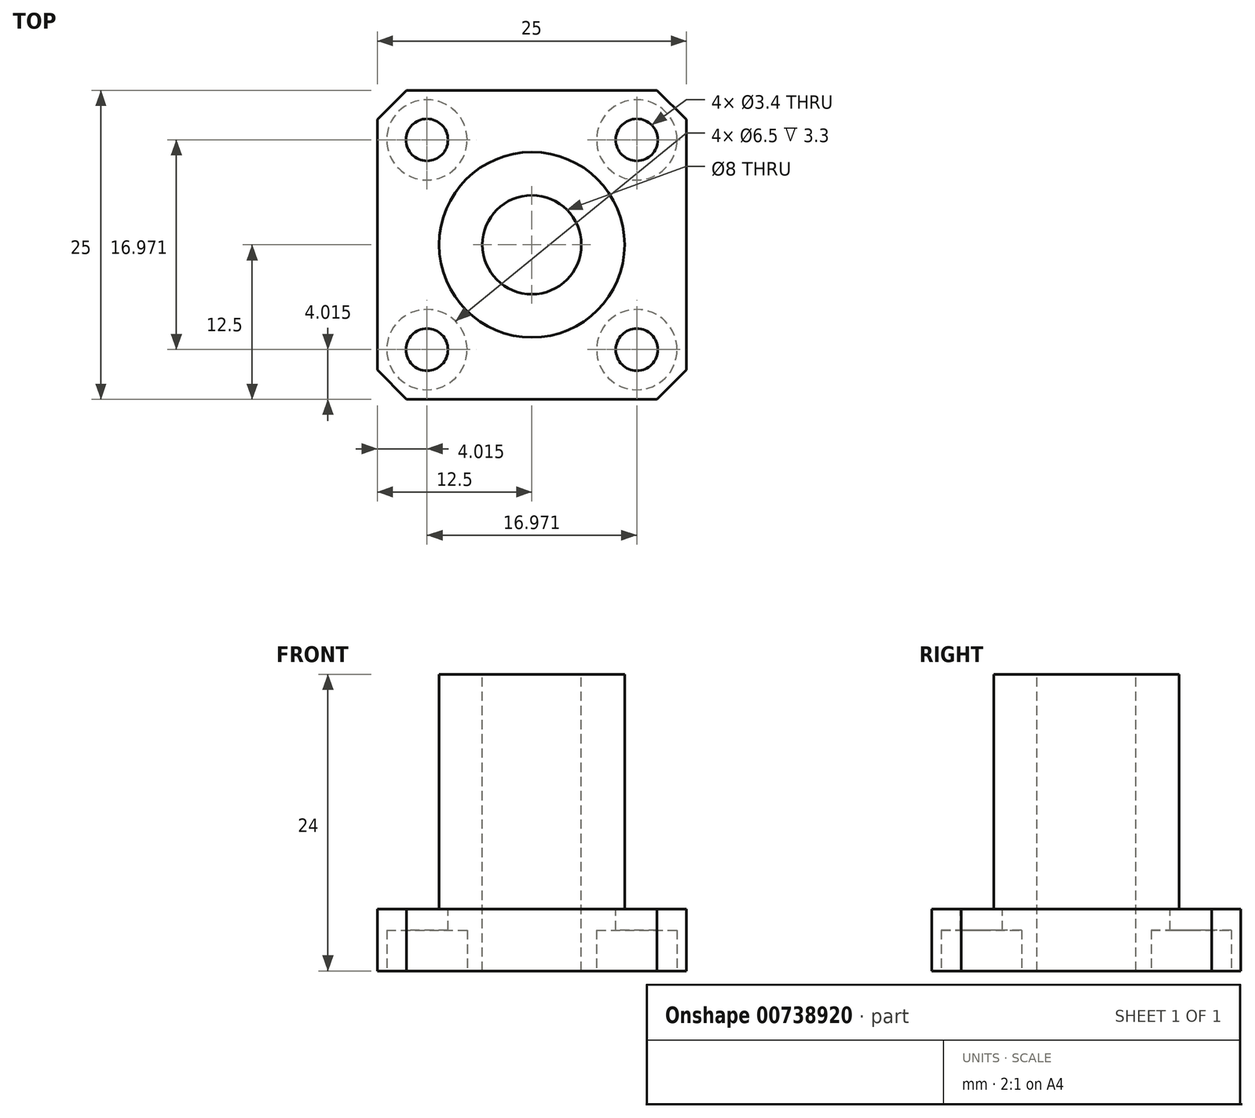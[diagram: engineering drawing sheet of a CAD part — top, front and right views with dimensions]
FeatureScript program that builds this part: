
annotation { "Feature Type Name" : "Feature", "Feature Type Description" : "" }
export const myFeature = defineFeature(function(context is Context, id is Id, definition is map)
    precondition{}
    {
        {
            var Q0;
            Q0=qCreatedBy(makeId("Top.planeOp"),FACE);
            var sketch = newSketch(context, id + "F0", { "sketchPlane" : qUnion([Q0])});
            skCircle(sketch, "E0", {"center": v(0, 0) * mm, "radius": 7.5 * mm});
            skCircle(sketch, "E1", {"center": v(0, 0) * mm, "radius": 4 * mm});
            skLineSegment(sketch, "E2.bottom", {"start": v(12.5, 12.5) * mm, "end": v(-12.5, 12.5) * mm});
            skLineSegment(sketch, "E2.top", {"start": v(12.5, -12.5) * mm, "end": v(-12.5, -12.5) * mm});
            skLineSegment(sketch, "E2.left", {"start": v(12.5, 12.5) * mm, "end": v(12.5, -12.5) * mm});
            skLineSegment(sketch, "E2.right", {"start": v(-12.5, 12.5) * mm, "end": v(-12.5, -12.5) * mm});
            skPoint(sketch, "E3", {"position": v(-8.49, -8.49) * mm});
            skPoint(sketch, "E4", {"position": v(8.49, 8.49) * mm});
            skPoint(sketch, "E5", {"position": v(-8.49, 8.49) * mm});
            skPoint(sketch, "E6", {"position": v(8.49, -8.49) * mm});
            skCircle(sketch, "E7", {"center": v(-8.49, 8.49) * mm, "radius": 1.7 * mm});
            skCircle(sketch, "E8", {"center": v(8.49, 8.49) * mm, "radius": 1.7 * mm});
            skCircle(sketch, "E9", {"center": v(8.49, -8.49) * mm, "radius": 1.7 * mm});
            skCircle(sketch, "E10", {"center": v(-8.49, -8.49) * mm, "radius": 1.7 * mm});
            skCircle(sketch, "E11", {"center": v(0, 0) * mm, "radius": 12 * mm, "construction": true});
            skLineSegment(sketch, "E12", {"start": v(-12.5, 12.5) * mm, "end": v(12.5, -12.5) * mm, "construction": true});
            skLineSegment(sketch, "E13", {"start": v(12.5, 12.5) * mm, "end": v(-12.5, -12.5) * mm, "construction": true});
            skSolve(sketch);
        }
        {
            var Q0;
            Q0=makeQuery(id+"F0.imprint","IMPRINT",FACE,{"disambiguationData":[TD([[makeQuery(id+"F0.imprint","IMPRINT",EDGE,{"derivedFrom":sQuery(id+"F0.wireOp",EDGE,"E0")}),1.0]])]});
            var Q1;
            Q1=makeQuery(id+"F0.imprint","IMPRINT",FACE,{"disambiguationData":[TD([[makeQuery(id+"F0.imprint","IMPRINT",EDGE,{"derivedFrom":sQuery(id+"F0.wireOp",EDGE,"E0")}),-1.0]])]});
            var Q2;
            {var subQ0=sQuery(id+"F0.wireOp",EDGE,"8207570f-5625-4c04-b362-0235c4b625b6.3.0");Q2=makeQuery(id+"F0.imprint","IMPRINT",FACE,{"disambiguationData":[TD([[makeQuery(id+"F0.imprint","IMPRINT",EDGE,{"derivedFrom":subQ0}),1.0]])]});}
            var Q3;
            {var subQ0=sQuery(id+"F0.wireOp",EDGE,"8207570f-5625-4c04-b362-0235c4b625b6.2.0");Q3=makeQuery(id+"F0.imprint","IMPRINT",FACE,{"disambiguationData":[TD([[makeQuery(id+"F0.imprint","IMPRINT",EDGE,{"derivedFrom":subQ0}),1.0]])]});}
            var Q4;
            {var subQ0=sQuery(id+"F0.wireOp",EDGE,"8207570f-5625-4c04-b362-0235c4b625b6.1.0");Q4=makeQuery(id+"F0.imprint","IMPRINT",FACE,{"disambiguationData":[TD([[makeQuery(id+"F0.imprint","IMPRINT",EDGE,{"derivedFrom":subQ0}),1.0]])]});}
            var Q5;
            {var subQ0=sQuery(id+"F0.wireOp",EDGE,"3kFZWS8e-WA2a-w8V8-dfVm-pTwxF5hzZJIQ");Q5=makeQuery(id+"F0.imprint","IMPRINT",FACE,{"disambiguationData":[TD([[makeQuery(id+"F0.imprint","IMPRINT",EDGE,{"derivedFrom":subQ0}),1.0]])]});}
            var Q6;
            {var subQ0=sQuery(id+"F0.wireOp",EDGE,"8207570f-5625-4c04-b362-0235c4b625b6.9.0");Q6=makeQuery(id+"F0.imprint","IMPRINT",FACE,{"disambiguationData":[TD([[makeQuery(id+"F0.imprint","IMPRINT",EDGE,{"derivedFrom":subQ0}),1.0]])]});}
            var Q7;
            {var subQ0=sQuery(id+"F0.wireOp",EDGE,"8207570f-5625-4c04-b362-0235c4b625b6.8.0");Q7=makeQuery(id+"F0.imprint","IMPRINT",FACE,{"disambiguationData":[TD([[makeQuery(id+"F0.imprint","IMPRINT",EDGE,{"derivedFrom":subQ0}),1.0]])]});}
            var Q8;
            {var subQ0=sQuery(id+"F0.wireOp",EDGE,"8207570f-5625-4c04-b362-0235c4b625b6.7.0");Q8=makeQuery(id+"F0.imprint","IMPRINT",FACE,{"disambiguationData":[TD([[makeQuery(id+"F0.imprint","IMPRINT",EDGE,{"derivedFrom":subQ0}),1.0]])]});}
            var Q9;
            {var subQ0=sQuery(id+"F0.wireOp",EDGE,"8207570f-5625-4c04-b362-0235c4b625b6.6.0");Q9=makeQuery(id+"F0.imprint","IMPRINT",FACE,{"disambiguationData":[TD([[makeQuery(id+"F0.imprint","IMPRINT",EDGE,{"derivedFrom":subQ0}),1.0]])]});}
            var Q10;
            {var subQ0=sQuery(id+"F0.wireOp",EDGE,"8207570f-5625-4c04-b362-0235c4b625b6.5.0");Q10=makeQuery(id+"F0.imprint","IMPRINT",FACE,{"disambiguationData":[TD([[makeQuery(id+"F0.imprint","IMPRINT",EDGE,{"derivedFrom":subQ0}),1.0]])]});}
            var Q11;
            {var subQ0=sQuery(id+"F0.wireOp",EDGE,"8207570f-5625-4c04-b362-0235c4b625b6.4.0");Q11=makeQuery(id+"F0.imprint","IMPRINT",FACE,{"disambiguationData":[TD([[makeQuery(id+"F0.imprint","IMPRINT",EDGE,{"derivedFrom":subQ0}),1.0]])]});}
            extrude(context, id + "F1", {"entities" : qUnion([Q0, Q1, Q2, Q3, Q4, Q5, Q6, Q7, Q8, Q9, Q10, Q11]), "oppositeDirection" : true, "depth" : 3.3 * mm, "offsetDistance" : 25 * mm});
        }
        {
            var Q0;
            Q0=makeQuery(id+"F0.imprint","IMPRINT",FACE,{"disambiguationData":[TD([[makeQuery(id+"F0.imprint","IMPRINT",EDGE,{"derivedFrom":sQuery(id+"F0.wireOp",EDGE,"a0KSDOvq-HjhY-bA0r-yQYG-hNEN9hOLSB91")}),1.0]])]});
            var Q1;
            Q1=makeQuery(id+"F0.imprint","IMPRINT",FACE,{"disambiguationData":[TD([[makeQuery(id+"F0.imprint","IMPRINT",EDGE,{"derivedFrom":sQuery(id+"F0.wireOp",EDGE,"E0")}),-1.0]])]});
            var Q2;
            Q2=makeQuery(id+"F0.imprint","IMPRINT",FACE,{"disambiguationData":[TD([[makeQuery(id+"F0.imprint","IMPRINT",EDGE,{"derivedFrom":sQuery(id+"F0.wireOp",EDGE,"KXfGxpAU-xU5Q-iWGt-S62b-6DmCXWTYX1BO")}),1.0]])]});
            var Q3;
            Q3=makeQuery(id+"F0.imprint","IMPRINT",FACE,{"disambiguationData":[TD([[makeQuery(id+"F0.imprint","IMPRINT",EDGE,{"derivedFrom":sQuery(id+"F0.wireOp",EDGE,"E0")}),1.0]])]});
            var Q4;
            {var subQ0=sQuery(id+"F0.wireOp",EDGE,"8207570f-5625-4c04-b362-0235c4b625b6.4.0");Q4=makeQuery(id+"F0.imprint","IMPRINT",FACE,{"disambiguationData":[TD([[makeQuery(id+"F0.imprint","IMPRINT",EDGE,{"derivedFrom":subQ0}),1.0]])]});}
            var Q5;
            {var subQ0=sQuery(id+"F0.wireOp",EDGE,"8207570f-5625-4c04-b362-0235c4b625b6.3.0");Q5=makeQuery(id+"F0.imprint","IMPRINT",FACE,{"disambiguationData":[TD([[makeQuery(id+"F0.imprint","IMPRINT",EDGE,{"derivedFrom":subQ0}),1.0]])]});}
            var Q6;
            {var subQ0=sQuery(id+"F0.wireOp",EDGE,"8207570f-5625-4c04-b362-0235c4b625b6.2.0");Q6=makeQuery(id+"F0.imprint","IMPRINT",FACE,{"disambiguationData":[TD([[makeQuery(id+"F0.imprint","IMPRINT",EDGE,{"derivedFrom":subQ0}),1.0]])]});}
            var Q7;
            {var subQ0=sQuery(id+"F0.wireOp",EDGE,"8207570f-5625-4c04-b362-0235c4b625b6.1.0");Q7=makeQuery(id+"F0.imprint","IMPRINT",FACE,{"disambiguationData":[TD([[makeQuery(id+"F0.imprint","IMPRINT",EDGE,{"derivedFrom":subQ0}),1.0]])]});}
            var Q8;
            {var subQ0=sQuery(id+"F0.wireOp",EDGE,"3kFZWS8e-WA2a-w8V8-dfVm-pTwxF5hzZJIQ");Q8=makeQuery(id+"F0.imprint","IMPRINT",FACE,{"disambiguationData":[TD([[makeQuery(id+"F0.imprint","IMPRINT",EDGE,{"derivedFrom":subQ0}),1.0]])]});}
            var Q9;
            {var subQ0=sQuery(id+"F0.wireOp",EDGE,"8207570f-5625-4c04-b362-0235c4b625b6.9.0");Q9=makeQuery(id+"F0.imprint","IMPRINT",FACE,{"disambiguationData":[TD([[makeQuery(id+"F0.imprint","IMPRINT",EDGE,{"derivedFrom":subQ0}),1.0]])]});}
            var Q10;
            {var subQ0=sQuery(id+"F0.wireOp",EDGE,"8207570f-5625-4c04-b362-0235c4b625b6.8.0");Q10=makeQuery(id+"F0.imprint","IMPRINT",FACE,{"disambiguationData":[TD([[makeQuery(id+"F0.imprint","IMPRINT",EDGE,{"derivedFrom":subQ0}),1.0]])]});}
            var Q11;
            {var subQ0=sQuery(id+"F0.wireOp",EDGE,"8207570f-5625-4c04-b362-0235c4b625b6.7.0");Q11=makeQuery(id+"F0.imprint","IMPRINT",FACE,{"disambiguationData":[TD([[makeQuery(id+"F0.imprint","IMPRINT",EDGE,{"derivedFrom":subQ0}),1.0]])]});}
            var Q12;
            {var subQ0=sQuery(id+"F0.wireOp",EDGE,"8207570f-5625-4c04-b362-0235c4b625b6.6.0");Q12=makeQuery(id+"F0.imprint","IMPRINT",FACE,{"disambiguationData":[TD([[makeQuery(id+"F0.imprint","IMPRINT",EDGE,{"derivedFrom":subQ0}),1.0]])]});}
            var Q13;
            {var subQ0=sQuery(id+"F0.wireOp",EDGE,"8207570f-5625-4c04-b362-0235c4b625b6.5.0");Q13=makeQuery(id+"F0.imprint","IMPRINT",FACE,{"disambiguationData":[TD([[makeQuery(id+"F0.imprint","IMPRINT",EDGE,{"derivedFrom":subQ0}),1.0]])]});}
            var Q14;
            Q14=makeQuery(id+"F0.imprint","IMPRINT",FACE,{"disambiguationData":[TD([[makeQuery(id+"F0.imprint","IMPRINT",EDGE,{"derivedFrom":sQuery(id+"F0.wireOp",EDGE,"nmBhYBad-r4Al-AfGY-MeFP-vAZGKTXBM8V1")}),1.0]])]});
            var Q15;
            Q15=makeQuery(id+"F0.imprint","IMPRINT",FACE,{"disambiguationData":[TD([[makeQuery(id+"F0.imprint","IMPRINT",EDGE,{"derivedFrom":sQuery(id+"F0.wireOp",EDGE,"MHbVS2jO-9CJP-TuAX-Z4Gs-fw21KT4Qcq4T")}),1.0]])]});
            extrude(context, id + "F2", {"entities" : qUnion([Q0, Q1, Q2, Q3, Q4, Q5, Q6, Q7, Q8, Q9, Q10, Q11, Q12, Q13, Q14, Q15]), "operationType" : NewBodyOperationType.ADD, "depth" : 1.7 * mm, "offsetDistance" : 25 * mm});
        }
        {
            var Q0;
            Q0=makeQuery(id+"F2.opExtrude","CAP_FACE",FACE,{"disambiguationData":[OSD([sQuery(id+"F0.wireOp",EDGE,"E1"),sQuery(id+"F0.wireOp",EDGE,"E2.bottom"),sQuery(id+"F0.wireOp",EDGE,"E2.top"),sQuery(id+"F0.wireOp",EDGE,"E2.left"),sQuery(id+"F0.wireOp",EDGE,"E2.right"),sQuery(id+"F0.wireOp",EDGE,"3kFZWS8e-WA2a-w8V8-dfVm-pTwxF5hzZJIQ"),sQuery(id+"F0.wireOp",EDGE,"d80TOzYt-lAmo-BJYU-geK1-gUax2p547Pt8"),sQuery(id+"F0.wireOp",EDGE,"dA3oxO1v-GvCN-ORGA-KpCW-h7Gg8ITBtu4o"),sQuery(id+"F0.wireOp",EDGE,"8207570f-5625-4c04-b362-0235c4b625b6.1.0"),sQuery(id+"F0.wireOp",EDGE,"8207570f-5625-4c04-b362-0235c4b625b6.1.1"),sQuery(id+"F0.wireOp",EDGE,"8207570f-5625-4c04-b362-0235c4b625b6.1.2"),sQuery(id+"F0.wireOp",EDGE,"8207570f-5625-4c04-b362-0235c4b625b6.2.0"),sQuery(id+"F0.wireOp",EDGE,"8207570f-5625-4c04-b362-0235c4b625b6.2.1"),sQuery(id+"F0.wireOp",EDGE,"8207570f-5625-4c04-b362-0235c4b625b6.2.2"),sQuery(id+"F0.wireOp",EDGE,"8207570f-5625-4c04-b362-0235c4b625b6.3.0"),sQuery(id+"F0.wireOp",EDGE,"8207570f-5625-4c04-b362-0235c4b625b6.3.1"),sQuery(id+"F0.wireOp",EDGE,"8207570f-5625-4c04-b362-0235c4b625b6.3.2"),sQuery(id+"F0.wireOp",EDGE,"8207570f-5625-4c04-b362-0235c4b625b6.4.0"),sQuery(id+"F0.wireOp",EDGE,"8207570f-5625-4c04-b362-0235c4b625b6.4.1"),sQuery(id+"F0.wireOp",EDGE,"8207570f-5625-4c04-b362-0235c4b625b6.4.2"),sQuery(id+"F0.wireOp",EDGE,"8207570f-5625-4c04-b362-0235c4b625b6.5.0"),sQuery(id+"F0.wireOp",EDGE,"8207570f-5625-4c04-b362-0235c4b625b6.5.1"),sQuery(id+"F0.wireOp",EDGE,"8207570f-5625-4c04-b362-0235c4b625b6.5.2"),sQuery(id+"F0.wireOp",EDGE,"8207570f-5625-4c04-b362-0235c4b625b6.6.0"),sQuery(id+"F0.wireOp",EDGE,"8207570f-5625-4c04-b362-0235c4b625b6.6.1"),sQuery(id+"F0.wireOp",EDGE,"8207570f-5625-4c04-b362-0235c4b625b6.6.2"),sQuery(id+"F0.wireOp",EDGE,"8207570f-5625-4c04-b362-0235c4b625b6.7.0"),sQuery(id+"F0.wireOp",EDGE,"8207570f-5625-4c04-b362-0235c4b625b6.7.1"),sQuery(id+"F0.wireOp",EDGE,"8207570f-5625-4c04-b362-0235c4b625b6.7.2"),sQuery(id+"F0.wireOp",EDGE,"8207570f-5625-4c04-b362-0235c4b625b6.8.0"),sQuery(id+"F0.wireOp",EDGE,"8207570f-5625-4c04-b362-0235c4b625b6.8.1"),sQuery(id+"F0.wireOp",EDGE,"8207570f-5625-4c04-b362-0235c4b625b6.8.2"),sQuery(id+"F0.wireOp",EDGE,"8207570f-5625-4c04-b362-0235c4b625b6.9.0"),sQuery(id+"F0.wireOp",EDGE,"8207570f-5625-4c04-b362-0235c4b625b6.9.1"),sQuery(id+"F0.wireOp",EDGE,"8207570f-5625-4c04-b362-0235c4b625b6.9.2"),sQuery(id+"F0.wireOp",EDGE,"E7"),sQuery(id+"F0.wireOp",EDGE,"E8"),sQuery(id+"F0.wireOp",EDGE,"E9"),sQuery(id+"F0.wireOp",EDGE,"E10")])],"isStart":false});
            var sketch = newSketch(context, id + "F3", { "sketchPlane" : qUnion([Q0])});
            skCircle(sketch, "E14", {"center": v(0, 0) * mm, "radius": 7.5 * mm});
            skSolve(sketch);
        }
        {
            var Q0;
            Q0=makeQuery(id+"F3.imprint","IMPRINT",FACE,{"disambiguationData":[TD([[makeQuery(id+"F3.imprint","IMPRINT",EDGE,{"derivedFrom":sQuery(id+"F3.wireOp",EDGE,"E14")}),1.0]])]});
            extrude(context, id + "F4", {"entities" : qUnion([Q0]), "operationType" : NewBodyOperationType.ADD, "depth" : 19 * mm, "offsetDistance" : 25 * mm});
        }
        {
            var Q0;
            Q0=makeQuery(id+"F2.opExtrude","CAP_FACE",FACE,{"disambiguationData":[OSD([sQuery(id+"F0.wireOp",EDGE,"E1"),sQuery(id+"F0.wireOp",EDGE,"E2.bottom"),sQuery(id+"F0.wireOp",EDGE,"E2.top"),sQuery(id+"F0.wireOp",EDGE,"E2.left"),sQuery(id+"F0.wireOp",EDGE,"E2.right"),sQuery(id+"F0.wireOp",EDGE,"E7"),sQuery(id+"F0.wireOp",EDGE,"E8"),sQuery(id+"F0.wireOp",EDGE,"E9"),sQuery(id+"F0.wireOp",EDGE,"E10")])],"isStart":false});
            var sketch = newSketch(context, id + "F5", { "sketchPlane" : qUnion([Q0])});
            skLineSegment(sketch, "E15", {"start": v(-22.63, 0) * mm, "end": v(0, 22.63) * mm});
            skLineSegment(sketch, "E16", {"start": v(0, 22.63) * mm, "end": v(22.63, 0) * mm});
            skLineSegment(sketch, "E17", {"start": v(22.63, 0) * mm, "end": v(0, -22.63) * mm});
            skLineSegment(sketch, "E18", {"start": v(0, -22.63) * mm, "end": v(-22.63, 0) * mm});
            skSolve(sketch);
        }
        {
            var Q0;
            {var subQ0=sQuery(id+"F5.wireOp",EDGE,"E15");var subQ1=makeQuery(id+"F2.opExtrude","CAP_EDGE",EDGE,{"disambiguationData":[OSD([sQuery(id+"F0.wireOp",EDGE,"E2.right")])],"isStart":false});var subQ2=makeQuery(id+"F5.imprint","INTERSECT",VERTEX,{"derivedFrom":[subQ1,subQ0]});Q0=makeQuery(id+"F5.imprint","IMPRINT",FACE,{"disambiguationData":[TD([[makeQuery(id+"F5.imprint","IMPRINT",EDGE,{"disambiguationData":[TD([[subQ2,-1.0]])],"derivedFrom":subQ0}),1.0]])]});}
            var Q1;
            {var subQ0=sQuery(id+"F5.wireOp",EDGE,"E18");var subQ1=makeQuery(id+"F2.opExtrude","CAP_EDGE",EDGE,{"disambiguationData":[OSD([sQuery(id+"F0.wireOp",EDGE,"E2.top")])],"isStart":false});var subQ2=makeQuery(id+"F5.imprint","INTERSECT",VERTEX,{"derivedFrom":[subQ1,subQ0]});Q1=makeQuery(id+"F5.imprint","IMPRINT",FACE,{"disambiguationData":[TD([[makeQuery(id+"F5.imprint","IMPRINT",EDGE,{"disambiguationData":[TD([[subQ2,-1.0]])],"derivedFrom":subQ0}),1.0]])]});}
            var Q2;
            {var subQ0=sQuery(id+"F5.wireOp",EDGE,"E17");var subQ1=makeQuery(id+"F2.opExtrude","CAP_EDGE",EDGE,{"disambiguationData":[OSD([sQuery(id+"F0.wireOp",EDGE,"E2.left")])],"isStart":false});var subQ2=makeQuery(id+"F5.imprint","INTERSECT",VERTEX,{"derivedFrom":[subQ1,subQ0]});Q2=makeQuery(id+"F5.imprint","IMPRINT",FACE,{"disambiguationData":[TD([[makeQuery(id+"F5.imprint","IMPRINT",EDGE,{"disambiguationData":[TD([[subQ2,-1.0]])],"derivedFrom":subQ0}),1.0]])]});}
            var Q3;
            {var subQ0=sQuery(id+"F5.wireOp",EDGE,"E16");var subQ1=makeQuery(id+"F2.opExtrude","CAP_EDGE",EDGE,{"disambiguationData":[OSD([sQuery(id+"F0.wireOp",EDGE,"E2.bottom")])],"isStart":false});var subQ2=makeQuery(id+"F5.imprint","INTERSECT",VERTEX,{"derivedFrom":[subQ1,subQ0]});Q3=makeQuery(id+"F5.imprint","IMPRINT",FACE,{"disambiguationData":[TD([[makeQuery(id+"F5.imprint","IMPRINT",EDGE,{"disambiguationData":[TD([[subQ2,-1.0]])],"derivedFrom":subQ0}),1.0]])]});}
            extrude(context, id + "F6", {"entities" : qUnion([Q0, Q1, Q2, Q3]), "operationType" : NewBodyOperationType.REMOVE, "oppositeDirection" : true, "depth" : 25 * mm, "offsetDistance" : 25 * mm});
        }
        {
            var Q0;
            Q0=makeQuery(id+"F1.opExtrude","CAP_FACE",FACE,{"disambiguationData":[OSD([sQuery(id+"F0.wireOp",EDGE,"E1"),sQuery(id+"F0.wireOp",EDGE,"E2.bottom"),sQuery(id+"F0.wireOp",EDGE,"E2.top"),sQuery(id+"F0.wireOp",EDGE,"E2.left"),sQuery(id+"F0.wireOp",EDGE,"E2.right"),sQuery(id+"F0.wireOp",EDGE,"E7"),sQuery(id+"F0.wireOp",EDGE,"E8"),sQuery(id+"F0.wireOp",EDGE,"E9"),sQuery(id+"F0.wireOp",EDGE,"E10")])],"isStart":false});
            var sketch = newSketch(context, id + "F7", { "sketchPlane" : qUnion([Q0])});
            skCircle(sketch, "E19", {"center": v(-8.49, 8.49) * mm, "radius": 3.25 * mm});
            skCircle(sketch, "E20", {"center": v(-8.49, -8.49) * mm, "radius": 3.25 * mm});
            skCircle(sketch, "E21", {"center": v(8.49, -8.49) * mm, "radius": 3.25 * mm});
            skCircle(sketch, "E22", {"center": v(8.49, 8.49) * mm, "radius": 3.25 * mm});
            skSolve(sketch);
        }
        {
            var Q0;
            Q0=makeQuery(id+"F7.imprint","IMPRINT",FACE,{"disambiguationData":[TD([[makeQuery(id+"F7.imprint","IMPRINT",EDGE,{"derivedFrom":sQuery(id+"F7.wireOp",EDGE,"E19")}),1.0]])]});
            var Q1;
            Q1=makeQuery(id+"F7.imprint","IMPRINT",FACE,{"disambiguationData":[TD([[makeQuery(id+"F7.imprint","IMPRINT",EDGE,{"derivedFrom":sQuery(id+"F7.wireOp",EDGE,"E22")}),1.0]])]});
            var Q2;
            Q2=makeQuery(id+"F7.imprint","IMPRINT",FACE,{"disambiguationData":[TD([[makeQuery(id+"F7.imprint","IMPRINT",EDGE,{"derivedFrom":sQuery(id+"F7.wireOp",EDGE,"E20")}),1.0]])]});
            var Q3;
            Q3=makeQuery(id+"F7.imprint","IMPRINT",FACE,{"disambiguationData":[TD([[makeQuery(id+"F7.imprint","IMPRINT",EDGE,{"derivedFrom":sQuery(id+"F7.wireOp",EDGE,"E21")}),1.0]])]});
            extrude(context, id + "F8", {"entities" : qUnion([Q0, Q1, Q2, Q3]), "operationType" : NewBodyOperationType.REMOVE, "oppositeDirection" : true, "depth" : 3.3 * mm, "offsetDistance" : 25 * mm});
        }
    });
